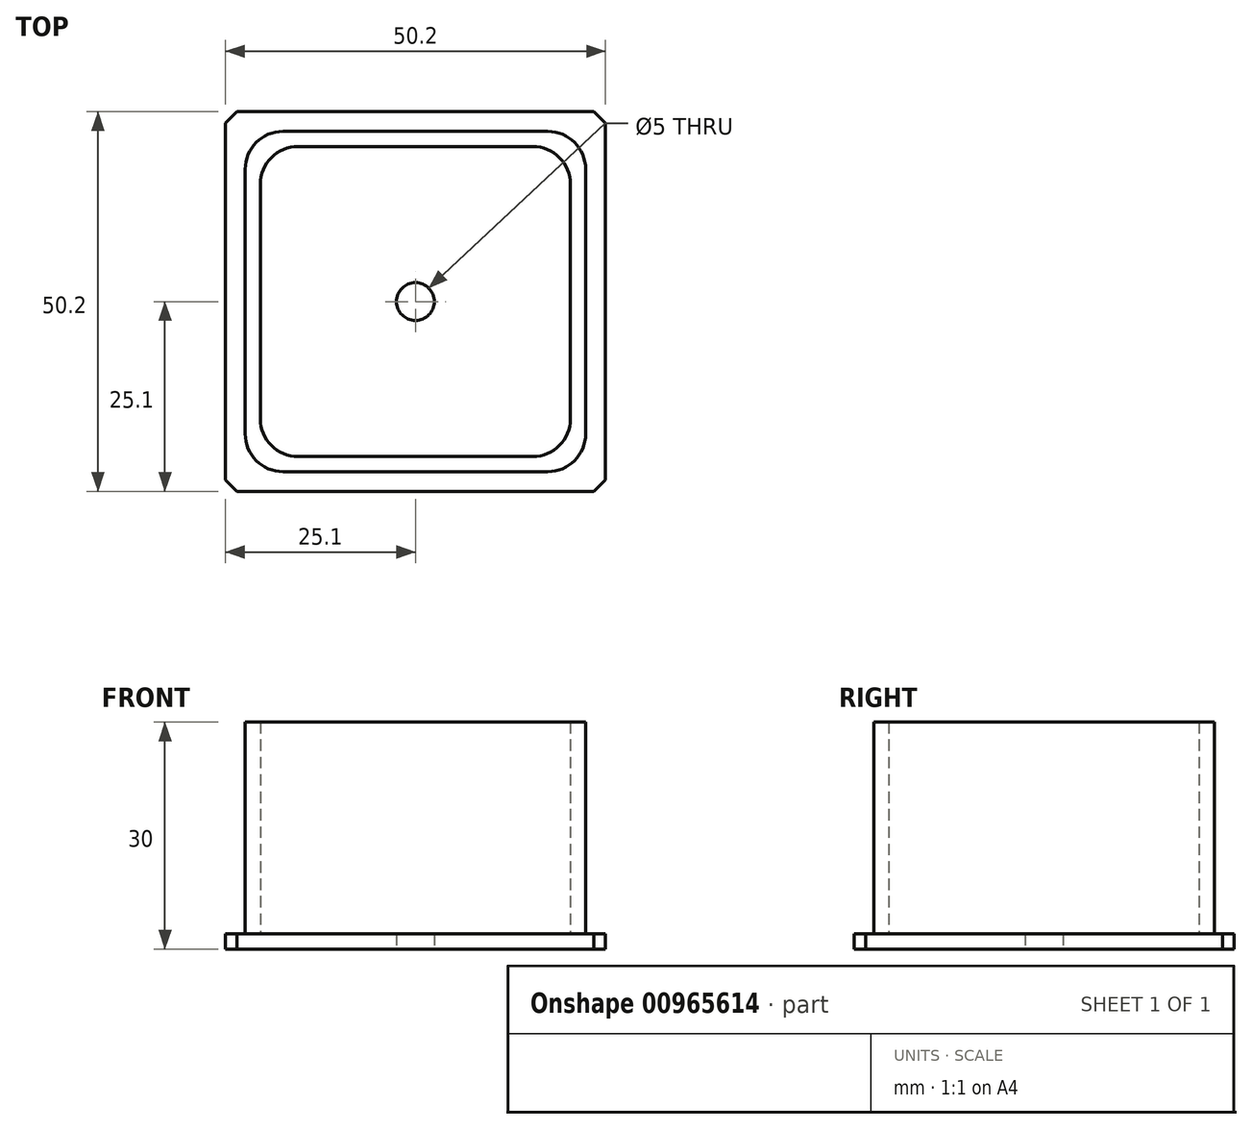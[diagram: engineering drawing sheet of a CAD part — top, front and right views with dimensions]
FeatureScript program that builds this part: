
annotation { "Feature Type Name" : "Feature", "Feature Type Description" : "" }
export const myFeature = defineFeature(function(context is Context, id is Id, definition is map)
    precondition{}
    {
        {
            var Q0;
            Q0=qCreatedBy(makeId("Top.planeOp"),FACE);
            var sketch = newSketch(context, id + "F0", { "sketchPlane" : qUnion([Q0])});
            skLineSegment(sketch, "E0.bottom", {"start": v(-25.1, 25.1) * mm, "end": v(25.1, 25.1) * mm});
            skLineSegment(sketch, "E0.top", {"start": v(-25.1, -25.1) * mm, "end": v(25.1, -25.1) * mm});
            skLineSegment(sketch, "E0.left", {"start": v(-25.1, 25.1) * mm, "end": v(-25.1, -25.1) * mm});
            skLineSegment(sketch, "E0.right", {"start": v(25.1, 25.1) * mm, "end": v(25.1, -25.1) * mm});
            skPoint(sketch, "E0.middle", {"position": v(0, 0) * mm});
            skLineSegment(sketch, "E1.bottom", {"start": v(-22.5, 22.5) * mm, "end": v(22.5, 22.5) * mm});
            skLineSegment(sketch, "E1.top", {"start": v(-22.5, -22.5) * mm, "end": v(22.5, -22.5) * mm});
            skLineSegment(sketch, "E1.left", {"start": v(-22.5, 22.5) * mm, "end": v(-22.5, -22.5) * mm});
            skLineSegment(sketch, "E1.right", {"start": v(22.5, 22.5) * mm, "end": v(22.5, -22.5) * mm});
            skCircle(sketch, "E2", {"center": v(0, 0) * mm, "radius": 2.5 * mm});
            skSolve(sketch);
        }
        {
            var Q0;
            Q0=makeQuery(id+"F0.imprint","IMPRINT",FACE,{"disambiguationData":[TD([[makeQuery(id+"F0.imprint","IMPRINT",EDGE,{"derivedFrom":sQuery(id+"F0.wireOp",EDGE,"E1.bottom")}),-1.0]])]});
            extrude(context, id + "F1", {"entities" : qUnion([Q0]), "depth" : 30 * mm, "offsetDistance" : 25 * mm});
        }
        {
            var Q0;
            Q0 = qSketchRegion(id + "F0", true);
            extrude(context, id + "F2", {"entities" : qUnion([Q0]), "operationType" : NewBodyOperationType.ADD, "depth" : 2 * mm, "offsetDistance" : 25 * mm});
        }
        {
            var Q0;
            Q0=makeQuery(id+"F1.opExtrude","CAP_FACE",FACE,{"disambiguationData":[OSD([sQuery(id+"F0.wireOp",EDGE,"E1.bottom"),sQuery(id+"F0.wireOp",EDGE,"E1.top"),sQuery(id+"F0.wireOp",EDGE,"E1.left"),sQuery(id+"F0.wireOp",EDGE,"E1.right"),sQuery(id+"F0.wireOp",EDGE,"E2")])],"isStart":false});
            var Q1;
            Q1=makeQuery(id+"F1.opExtrude","SWEPT_FACE",FACE,{"disambiguationData":[OSD([sQuery(id+"F0.wireOp",EDGE,"E2")])]});
            shell(context, id + "F3", {"entities" : qUnion([Q0, Q1]), "thickness" : 2 * mm});
        }
        {
            var Q0;
            Q0=makeQuery(id+"F1.opExtrude","SWEPT_EDGE",EDGE,{"disambiguationData":[OSD([sQuery(id+"F0.wireOp",EDGE,"E1.top"),sQuery(id+"F0.wireOp",EDGE,"E1.left")])]});
            var Q1;
            Q1=makeQuery(id+"F1.opExtrude","SWEPT_EDGE",EDGE,{"disambiguationData":[OSD([sQuery(id+"F0.wireOp",EDGE,"E1.top"),sQuery(id+"F0.wireOp",EDGE,"E1.right")])]});
            var Q2;
            Q2=makeQuery(id+"F1.opExtrude","SWEPT_EDGE",EDGE,{"disambiguationData":[OSD([sQuery(id+"F0.wireOp",EDGE,"E1.bottom"),sQuery(id+"F0.wireOp",EDGE,"E1.right")])]});
            var Q3;
            Q3=makeQuery(id+"F1.opExtrude","SWEPT_EDGE",EDGE,{"disambiguationData":[OSD([sQuery(id+"F0.wireOp",EDGE,"E1.bottom"),sQuery(id+"F0.wireOp",EDGE,"E1.left")])]});
            var Q4;
            Q4=makeQuery(id+"F3.opShell","OFFSET_EDGE",EDGE,{"disambiguationData":[OSD([sQuery(id+"F0.wireOp",EDGE,"E1.bottom"),sQuery(id+"F0.wireOp",EDGE,"E1.right")])]});
            var Q5;
            Q5=makeQuery(id+"F3.opShell","OFFSET_EDGE",EDGE,{"disambiguationData":[OSD([sQuery(id+"F0.wireOp",EDGE,"E1.bottom"),sQuery(id+"F0.wireOp",EDGE,"E1.left")])]});
            var Q6;
            Q6=makeQuery(id+"F3.opShell","OFFSET_EDGE",EDGE,{"disambiguationData":[OSD([sQuery(id+"F0.wireOp",EDGE,"E1.top"),sQuery(id+"F0.wireOp",EDGE,"E1.left")])]});
            var Q7;
            Q7=makeQuery(id+"F3.opShell","OFFSET_EDGE",EDGE,{"disambiguationData":[OSD([sQuery(id+"F0.wireOp",EDGE,"E1.top"),sQuery(id+"F0.wireOp",EDGE,"E1.right")])]});
            fillet(context, id + "F4", {"entities" : qUnion([Q0, Q1, Q2, Q3, Q4, Q5, Q6, Q7]), "radius" : 5 * mm, "tangentPropagation" : true, "allowEdgeOverflow" : false});
        }
        {
            var Q0;
            Q0=makeQuery(id+"F2.opExtrude","SWEPT_EDGE",EDGE,{"disambiguationData":[OSD([sQuery(id+"F0.wireOp",EDGE,"E0.bottom"),sQuery(id+"F0.wireOp",EDGE,"E0.right")])]});
            var Q1;
            Q1=makeQuery(id+"F2.opExtrude","SWEPT_EDGE",EDGE,{"disambiguationData":[OSD([sQuery(id+"F0.wireOp",EDGE,"E0.top"),sQuery(id+"F0.wireOp",EDGE,"E0.right")])]});
            var Q2;
            Q2=makeQuery(id+"F2.opExtrude","SWEPT_EDGE",EDGE,{"disambiguationData":[OSD([sQuery(id+"F0.wireOp",EDGE,"E0.bottom"),sQuery(id+"F0.wireOp",EDGE,"E0.left")])]});
            var Q3;
            Q3=makeQuery(id+"F2.opExtrude","SWEPT_EDGE",EDGE,{"disambiguationData":[OSD([sQuery(id+"F0.wireOp",EDGE,"E0.top"),sQuery(id+"F0.wireOp",EDGE,"E0.left")])]});
            chamfer(context, id + "F5", {"entities" : qUnion([Q0, Q1, Q2, Q3]), "width" : 1.5 * mm, "tangentPropagation" : true});
        }
    });
